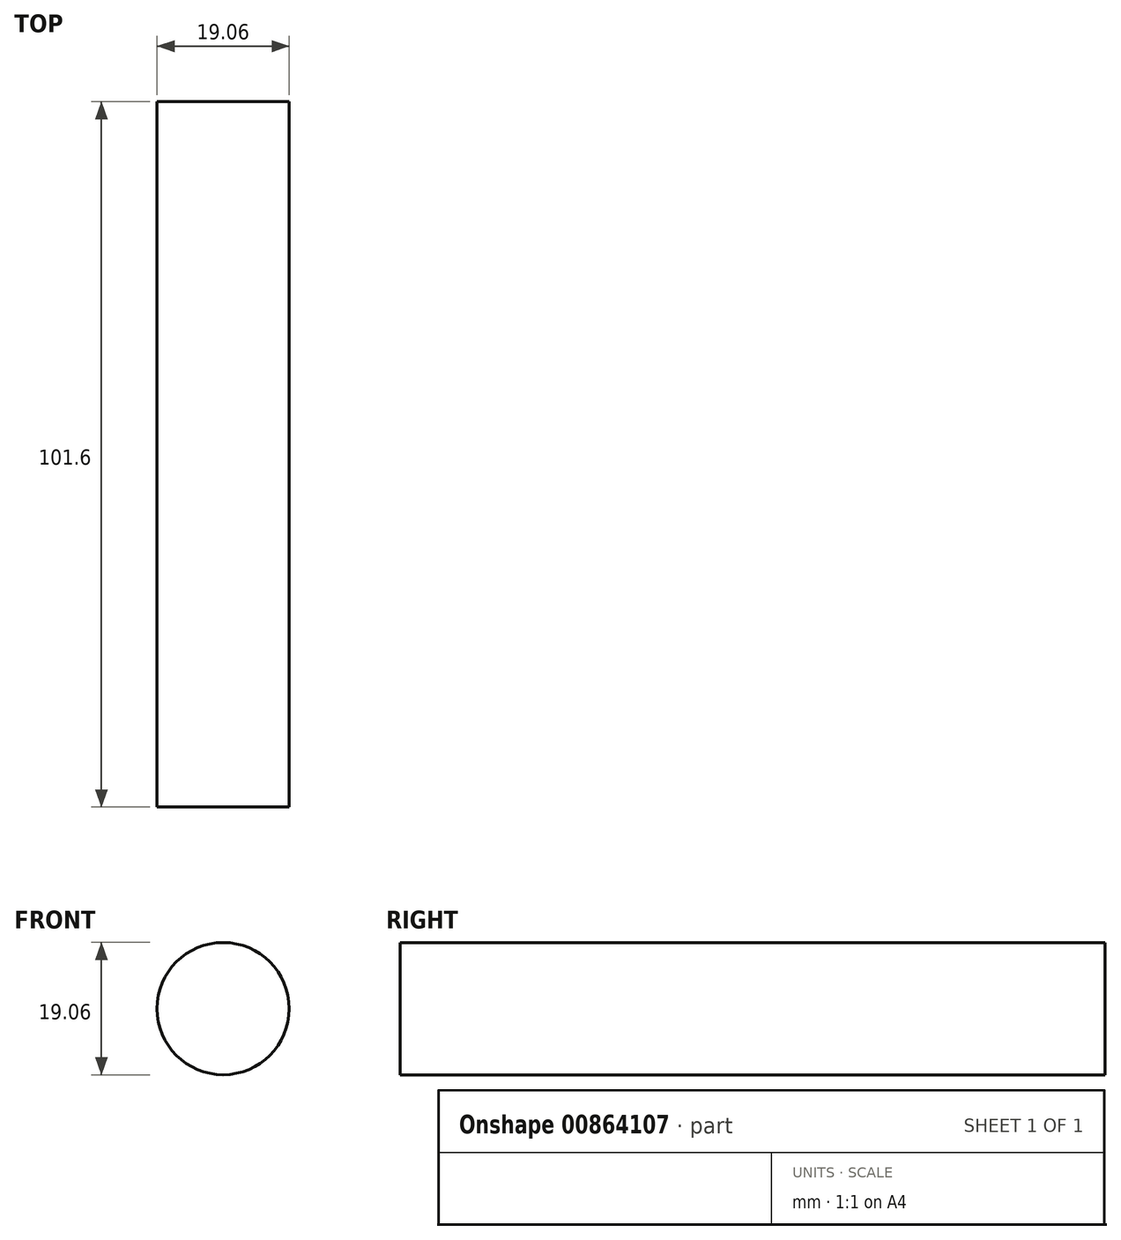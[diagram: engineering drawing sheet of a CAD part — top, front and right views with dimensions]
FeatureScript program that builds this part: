
annotation { "Feature Type Name" : "Feature", "Feature Type Description" : "" }
export const myFeature = defineFeature(function(context is Context, id is Id, definition is map)
    precondition{}
    {
        {
            var Q0;
            Q0=qCreatedBy(makeId("Front.planeOp"),FACE);
            var sketch = newSketch(context, id + "F0", { "sketchPlane" : qUnion([Q0])});
            skCircle(sketch, "E0", {"center": v(0, 0) * mm, "radius": 9.53 * mm});
            skSolve(sketch);
        }
        {
            var Q0;
            Q0=makeQuery(id+"F0.imprint","IMPRINT",FACE,{"disambiguationData":[TD([[makeQuery(id+"F0.imprint","IMPRINT",EDGE,{"derivedFrom":sQuery(id+"F0.wireOp",EDGE,"E0")}),1.0]])]});
            extrude(context, id + "F1", {"entities" : qUnion([Q0]), "depth" : 101.6 * mm, "offsetDistance" : 25.4 * mm});
        }
    });
